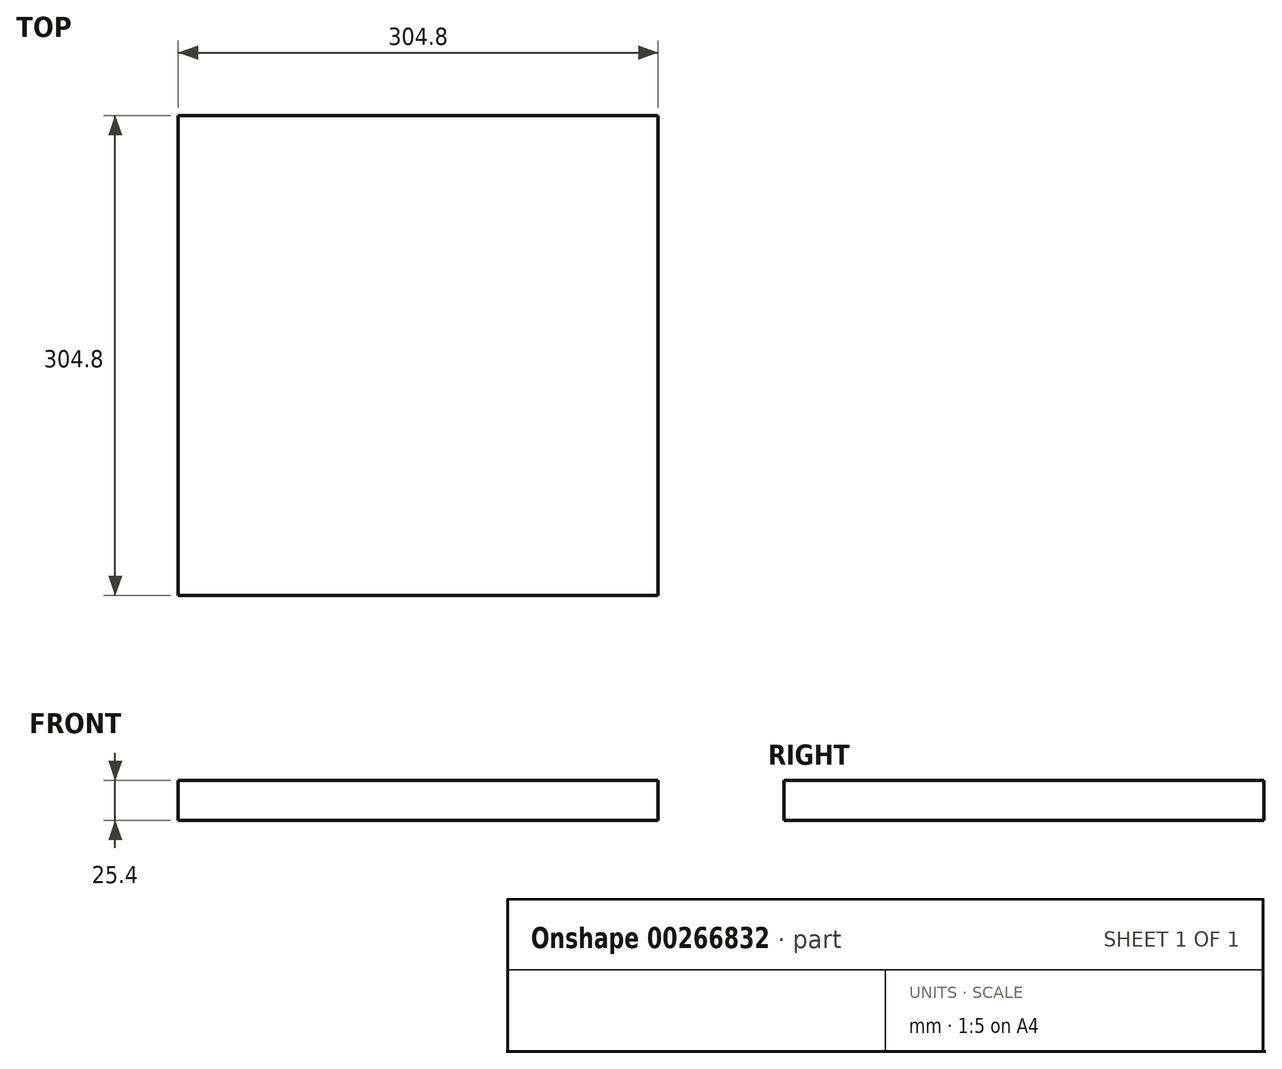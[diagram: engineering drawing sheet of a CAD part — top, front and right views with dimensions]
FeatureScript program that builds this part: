
annotation { "Feature Type Name" : "Feature", "Feature Type Description" : "" }
export const myFeature = defineFeature(function(context is Context, id is Id, definition is map)
    precondition{}
    {
        {
            var Q0;
            Q0=qCreatedBy(makeId("Top.planeOp"),FACE);
            var sketch = newSketch(context, id + "F0", { "sketchPlane" : qUnion([Q0])});
            skLineSegment(sketch, "E0.bottom", {"start": v(152.4, -152.4) * mm, "end": v(-152.4, -152.4) * mm});
            skLineSegment(sketch, "E0.top", {"start": v(152.4, 152.4) * mm, "end": v(-152.4, 152.4) * mm});
            skLineSegment(sketch, "E0.left", {"start": v(152.4, -152.4) * mm, "end": v(152.4, 152.4) * mm});
            skLineSegment(sketch, "E0.right", {"start": v(-152.4, -152.4) * mm, "end": v(-152.4, 152.4) * mm});
            skPoint(sketch, "E0.middle", {"position": v(0, 0) * mm});
            skSolve(sketch);
        }
        {
            var Q0;
            Q0=makeQuery(id+"F0.imprint","IMPRINT",FACE,{"disambiguationData":[TD([[makeQuery(id+"F0.imprint","IMPRINT",EDGE,{"derivedFrom":sQuery(id+"F0.wireOp",EDGE,"E0.bottom")}),-1.0]])]});
            extrude(context, id + "F1", {"entities" : qUnion([Q0]), "depth" : 25.4 * mm});
        }
    });
